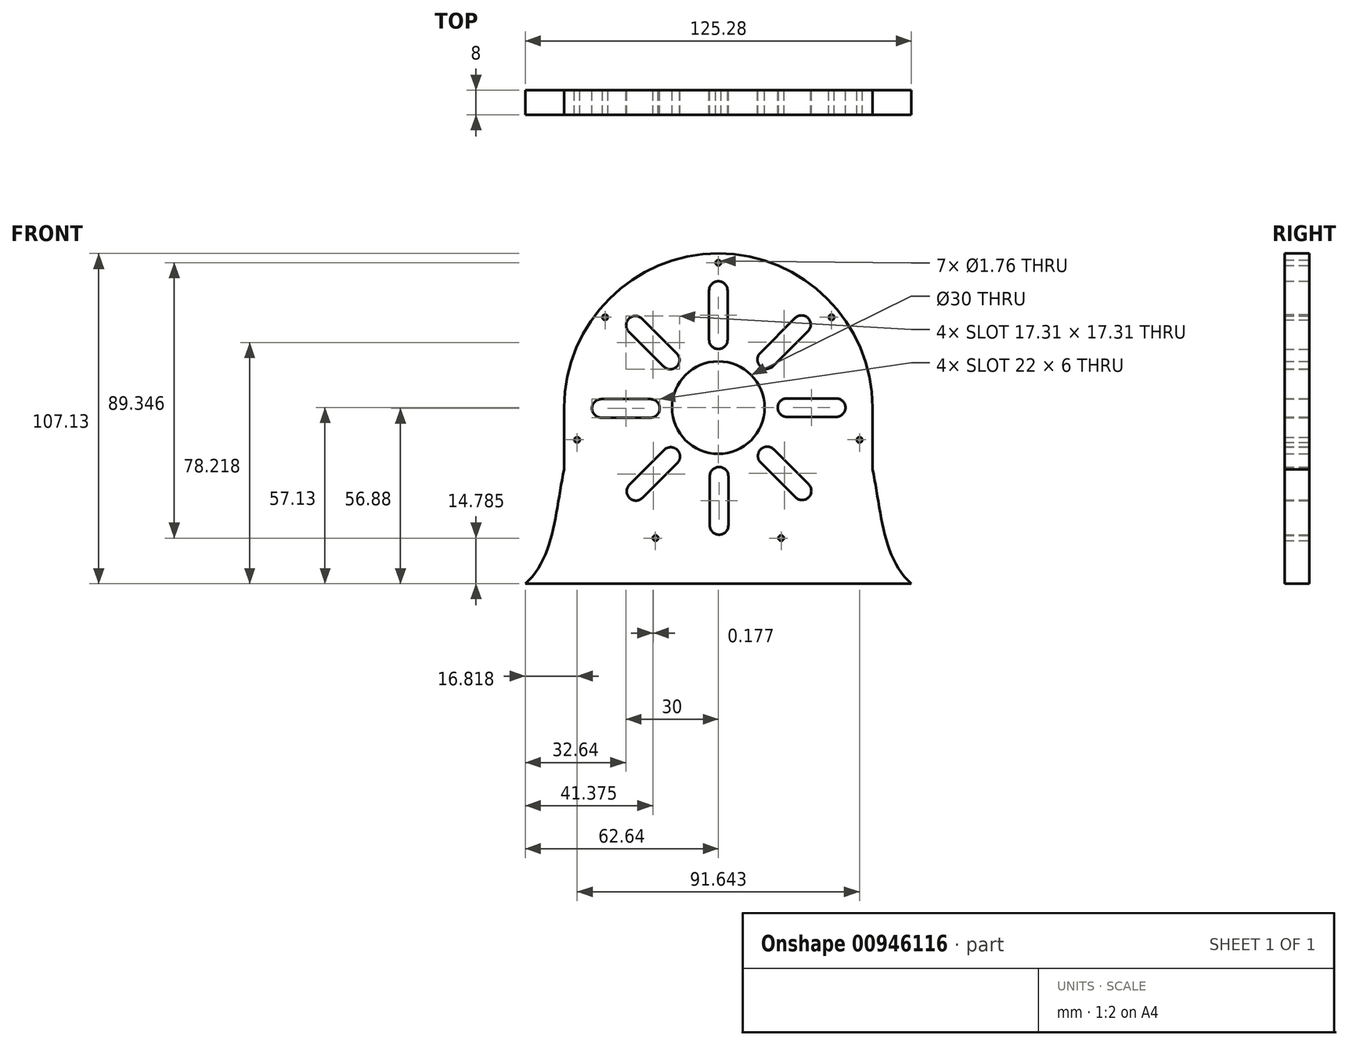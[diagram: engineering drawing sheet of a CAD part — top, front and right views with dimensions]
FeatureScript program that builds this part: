
annotation { "Feature Type Name" : "Feature", "Feature Type Description" : "" }
export const myFeature = defineFeature(function(context is Context, id is Id, definition is map)
    precondition{}
    {
        {
            var Q0;
            Q0=qCreatedBy(makeId("Front.planeOp"),FACE);
            var sketch = newSketch(context, id + "F0", { "sketchPlane" : qUnion([Q0])});
            skArc(sketch, "E0", {"start": v(50, 0) * mm, "mid": v(0, 50) * mm, "end": v(-50, 0) * mm});
            skLineSegment(sketch, "E1", {"start": v(-50, 0) * mm, "end": v(-50, -20) * mm});
            skLineSegment(sketch, "E2", {"start": v(-62.64, -57.13) * mm, "end": v(0, -57.13) * mm});
            skLineSegment(sketch, "E3.MirrorCS", {"start": v(62.64, -57.13) * mm, "end": v(0, -57.13) * mm});
            skLineSegment(sketch, "E4.MirrorCS", {"start": v(50, 0) * mm, "end": v(50, -20) * mm});
            skFitSpline(sketch, "E5", {"points": [v(-50, -20) * mm, v(-62.64, -57.13) * mm], "startDerivative": vector(-8.6, -38.71) * mm, "endDerivative": vector(-28.77, -25) * mm});
            skFitSpline(sketch, "E6.MirrorCS", {"points": [v(50, -20) * mm, v(62.64, -57.13) * mm], "startDerivative": vector(8.6, -38.71) * mm, "endDerivative": vector(28.77, -25) * mm});
            skCircle(sketch, "E7", {"center": v(0, 0) * mm, "radius": 15 * mm});
            skArc(sketch, "E8", {"start": v(3, 38) * mm, "mid": v(0, 41) * mm, "end": v(-3, 38) * mm});
            skArc(sketch, "E9", {"start": v(-3, 22) * mm, "mid": v(0, 19) * mm, "end": v(3, 22) * mm});
            skLineSegment(sketch, "E10", {"start": v(-3, 38) * mm, "end": v(-3, 22) * mm});
            skLineSegment(sketch, "E11", {"start": v(3, 38) * mm, "end": v(3, 22) * mm});
            skLineSegment(sketch, "E12.1.0", {"start": v(-24.8, 28.87) * mm, "end": v(-13.49, 17.55) * mm});
            skArc(sketch, "E12.1.1", {"start": v(-24.8, 28.87) * mm, "mid": v(-29.04, 28.87) * mm, "end": v(-29.04, 24.62) * mm});
            skLineSegment(sketch, "E12.1.2", {"start": v(-29.04, 24.62) * mm, "end": v(-17.73, 13.31) * mm});
            skArc(sketch, "E12.1.3", {"start": v(-17.73, 13.31) * mm, "mid": v(-13.49, 13.31) * mm, "end": v(-13.49, 17.55) * mm});
            skLineSegment(sketch, "E12.2.0", {"start": v(-38, 2.75) * mm, "end": v(-22, 2.75) * mm});
            skArc(sketch, "E12.2.1", {"start": v(-38, 2.75) * mm, "mid": v(-41, -0.25) * mm, "end": v(-38, -3.25) * mm});
            skLineSegment(sketch, "E12.2.2", {"start": v(-38, -3.25) * mm, "end": v(-22, -3.25) * mm});
            skArc(sketch, "E12.2.3", {"start": v(-22, -3.25) * mm, "mid": v(-19, -0.25) * mm, "end": v(-22, 2.75) * mm});
            skLineSegment(sketch, "E12.3.0", {"start": v(-28.87, -25.05) * mm, "end": v(-17.55, -13.74) * mm});
            skArc(sketch, "E12.3.1", {"start": v(-28.87, -25.05) * mm, "mid": v(-28.87, -29.3) * mm, "end": v(-24.62, -29.3) * mm});
            skLineSegment(sketch, "E12.3.2", {"start": v(-24.62, -29.3) * mm, "end": v(-13.31, -17.98) * mm});
            skArc(sketch, "E12.3.3", {"start": v(-13.31, -17.98) * mm, "mid": v(-13.31, -13.74) * mm, "end": v(-17.55, -13.74) * mm});
            skLineSegment(sketch, "E12.4.0", {"start": v(-2.75, -38.25) * mm, "end": v(-2.75, -22.25) * mm});
            skArc(sketch, "E12.4.1", {"start": v(-2.75, -38.25) * mm, "mid": v(0.25, -41.25) * mm, "end": v(3.25, -38.25) * mm});
            skLineSegment(sketch, "E12.4.2", {"start": v(3.25, -38.25) * mm, "end": v(3.25, -22.25) * mm});
            skArc(sketch, "E12.4.3", {"start": v(3.25, -22.25) * mm, "mid": v(0.25, -19.25) * mm, "end": v(-2.75, -22.25) * mm});
            skLineSegment(sketch, "E12.5.0", {"start": v(25.05, -29.12) * mm, "end": v(13.74, -17.8) * mm});
            skArc(sketch, "E12.5.1", {"start": v(25.05, -29.12) * mm, "mid": v(29.3, -29.12) * mm, "end": v(29.3, -24.87) * mm});
            skLineSegment(sketch, "E12.5.2", {"start": v(29.3, -24.87) * mm, "end": v(17.98, -13.56) * mm});
            skArc(sketch, "E12.5.3", {"start": v(17.98, -13.56) * mm, "mid": v(13.74, -13.56) * mm, "end": v(13.74, -17.8) * mm});
            skLineSegment(sketch, "E12.6.0", {"start": v(38.25, -3) * mm, "end": v(22.25, -3) * mm});
            skArc(sketch, "E12.6.1", {"start": v(38.25, -3) * mm, "mid": v(41.25, 0) * mm, "end": v(38.25, 3) * mm});
            skLineSegment(sketch, "E12.6.2", {"start": v(38.25, 3) * mm, "end": v(22.25, 3) * mm});
            skArc(sketch, "E12.6.3", {"start": v(22.25, 3) * mm, "mid": v(19.25, 0) * mm, "end": v(22.25, -3) * mm});
            skLineSegment(sketch, "E12.7.0", {"start": v(29.12, 24.8) * mm, "end": v(17.8, 13.49) * mm});
            skArc(sketch, "E12.7.1", {"start": v(29.12, 24.8) * mm, "mid": v(29.12, 29.04) * mm, "end": v(24.87, 29.04) * mm});
            skLineSegment(sketch, "E12.7.2", {"start": v(24.87, 29.04) * mm, "end": v(13.56, 17.73) * mm});
            skArc(sketch, "E12.7.3", {"start": v(13.56, 17.73) * mm, "mid": v(13.56, 13.49) * mm, "end": v(17.8, 13.49) * mm});
            skPoint(sketch, "E12.center", {"position": v(0.12, -0.12) * mm});
            skCircle(sketch, "E13", {"center": v(0, 0) * mm, "radius": 44 * mm, "construction": true});
            skCircle(sketch, "E14", {"center": v(0, 47) * mm, "radius": 0.88 * mm});
            skPoint(sketch, "E14.centerSnap0", {"position": v(0, 50) * mm});
            skCircle(sketch, "E15.1.0", {"center": v(-36.75, 29.3) * mm, "radius": 0.88 * mm});
            skCircle(sketch, "E15.2.0", {"center": v(-45.82, -10.46) * mm, "radius": 0.88 * mm});
            skCircle(sketch, "E15.3.0", {"center": v(-20.4, -42.35) * mm, "radius": 0.88 * mm});
            skCircle(sketch, "E15.4.0", {"center": v(20.4, -42.35) * mm, "radius": 0.88 * mm});
            skCircle(sketch, "E15.5.0", {"center": v(45.82, -10.46) * mm, "radius": 0.88 * mm});
            skCircle(sketch, "E15.6.0", {"center": v(36.75, 29.3) * mm, "radius": 0.88 * mm});
            skSolve(sketch);
        }
        {
            var Q0;
            Q0=qSketchRegion(id+"F0",true);
            extrude(context, id + "F1", {"entities" : qUnion([Q0]), "depth" : 8 * mm});
        }
    });
